# Revit family: Potentialausgleichsschiene für Kleinanlagen
name_source: partatom
category: Generic Models
revit_build: Autodesk Revit 2015 (Build: 20140606_1530(x64)
units: mm (PartAtom-declared; Revit-internal decimal feet)

## types (1)
- 1809 BG
    Article Type = 1809 BG
    GTIN = 4012195378372
    Height = 29 mm  [stored 0.0951444 ft]
    Height 1 = 6 mm  [stored 0.019685 ft]
    Length = 72 mm  [stored 0.23622 ft]
    Length 1 = 55 mm  [stored 0.180446 ft]
    Length 2 = 66 mm  [stored 0.216535 ft]
    Manufacturer = OBO Bettermann
    Manufacturer Art.No. = 5015502
    Material = Steel, Galvanized
    Material 2 = Brass, Soft Yellow
    Material 3 = Polystyrene
    URL = http://www.obo-bettermann.com
    Width = 45 mm
    Width 1 = 14 mm  [stored 0.0459318 ft]

note: [stored X ft] marks values corroborated as IEEE doubles in the binary element streams (Revit-internal decimal feet)

## geometry (parser evidence)
native form markers: Sweep x2
no freeform markers — native parametric forms only
